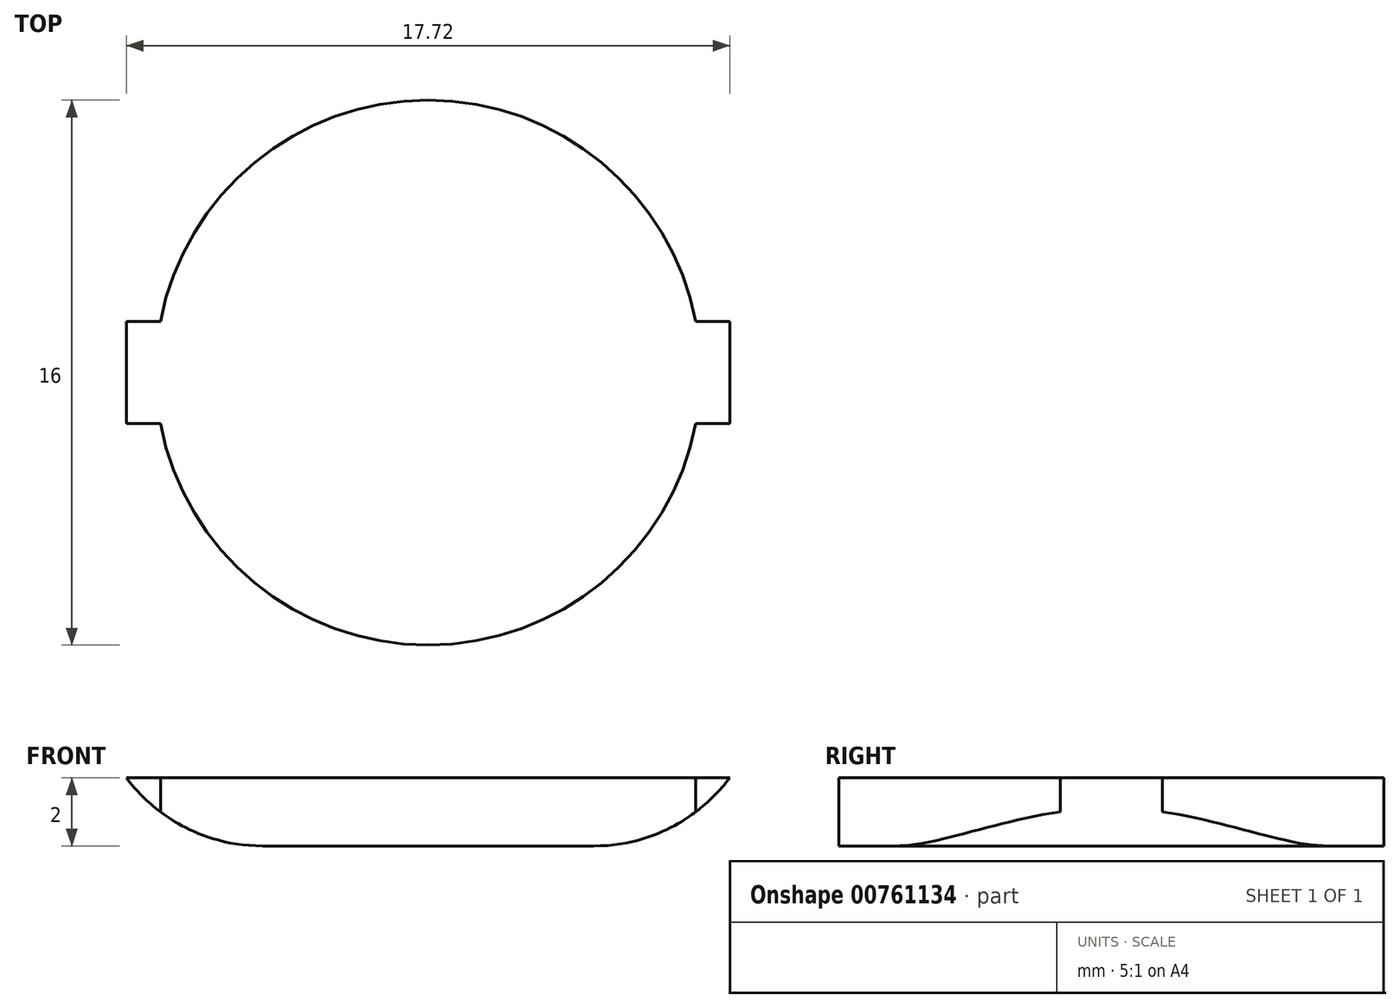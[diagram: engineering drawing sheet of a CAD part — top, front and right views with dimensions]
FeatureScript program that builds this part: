
annotation { "Feature Type Name" : "Feature", "Feature Type Description" : "" }
export const myFeature = defineFeature(function(context is Context, id is Id, definition is map)
    precondition{}
    {
        {
            var Q0;
            Q0=qCreatedBy(makeId("Top.planeOp"),FACE);
            var sketch = newSketch(context, id + "F0", { "sketchPlane" : qUnion([Q0])});
            skCircle(sketch, "E0", {"center": v(0, 0) * mm, "radius": 8 * mm});
            skLineSegment(sketch, "E1", {"start": v(7.86, 1.5) * mm, "end": v(8.86, 1.5) * mm});
            skLineSegment(sketch, "E2", {"start": v(8.86, 1.5) * mm, "end": v(8.86, -1.5) * mm});
            skLineSegment(sketch, "E3", {"start": v(8.86, -1.5) * mm, "end": v(7.86, -1.5) * mm});
            skLineSegment(sketch, "E4", {"start": v(-7.86, 1.5) * mm, "end": v(-8.86, 1.5) * mm});
            skLineSegment(sketch, "E5", {"start": v(-8.86, 1.5) * mm, "end": v(-8.86, -1.5) * mm});
            skLineSegment(sketch, "E6", {"start": v(-8.86, -1.5) * mm, "end": v(-7.86, -1.5) * mm});
            skLineSegment(sketch, "E7", {"start": v(0, -8) * mm, "end": v(0, 8) * mm});
            skLineSegment(sketch, "E8", {"start": v(-8.86, 0) * mm, "end": v(8.86, 0) * mm});
            skSolve(sketch);
        }
        {
            var Q0;
            Q0 = qSketchRegion(id + "F0", true);
            extrude(context, id + "F1", {"entities" : qUnion([Q0]), "depth" : 2 * mm, "offsetDistance" : 25.4 * mm});
        }
        {
            var Q0;
            Q0=makeQuery(id+"F1.opExtrude","CAP_EDGE",EDGE,{"disambiguationData":[OSD([sQuery(id+"F0.wireOp",EDGE,"E5")])],"isStart":true});
            var Q1;
            Q1=makeQuery(id+"F1.opExtrude","CAP_EDGE",EDGE,{"disambiguationData":[OSD([sQuery(id+"F0.wireOp",EDGE,"E2")])],"isStart":true});
            fillet(context, id + "F2", {"entities" : qUnion([Q0, Q1]), "radius" : 5 * mm, "tangentPropagation" : true, "allowEdgeOverflow" : false});
        }
    });
